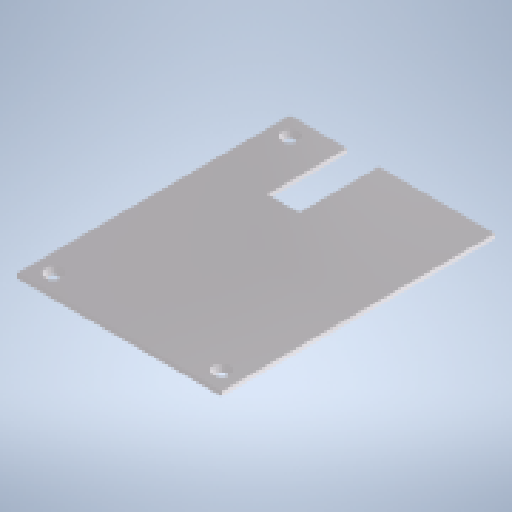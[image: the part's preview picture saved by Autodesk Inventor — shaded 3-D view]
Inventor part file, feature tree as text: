
AUTODESK INVENTOR PART (.ipt)
format: ipt  version: 2025 (Build 290162010, 162A)  size: 174,592 bytes
history: native  units: mm
features: sketch x2, extrude x1, hole x1, other x1
ambient origin geometry x8: Origin, YZ Plane, XZ Plane, XY Plane, X Axis, Y Axis, Z Axis, Center Point
bodies: Volumenkörper1 (feature_tree)
feature tree (5):
  extrude  "Extrusion1"  Depth=35.0mm
  hole  "Bohrung1"  [1 undecoded]
  sketch  "Skizze1"  dims[d0=14.0mm d1=35.0mm]
  sketch  "Skizze2"  dims[d2=25.0mm d3=0.0mm d4=0.0mm d5=8.0mm d6=8.0mm d7=8.0mm d8=8.0mm d9=3.4mm d10=8.0mm d11=6.3mm d12=2.0mm d13=90.0deg d14=8.0mm d15=20.594885mm]
  other  "item_47308_blech-al-2mm-naturfarben_120_90_high_1_1:1"
note: 1 required parameter value undecoded (feature->parameter linkage not recoverable at this tier; creation-order binding heuristic only, values carry confidence <= 0.55)
